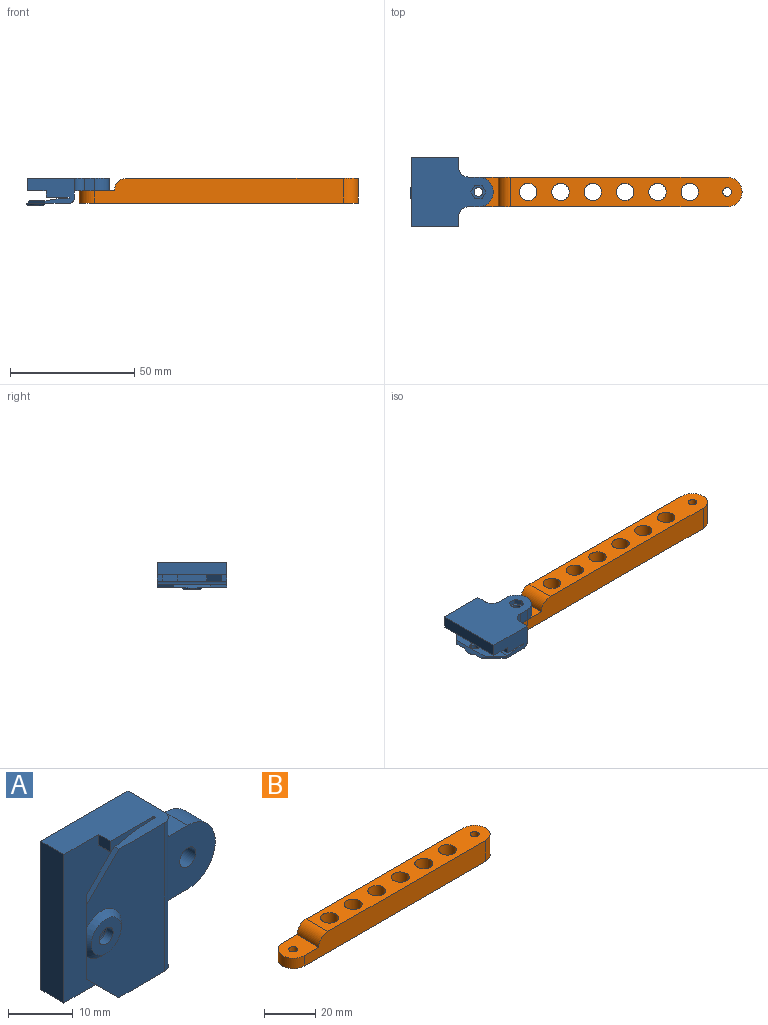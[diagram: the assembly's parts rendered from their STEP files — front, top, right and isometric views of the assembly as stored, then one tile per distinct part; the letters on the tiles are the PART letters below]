
ASSEMBLY  parts=2 mates=1
PART A: 40 faces, bbox 34x11x28 mm
  f0: plane 19x10mm, normal (0,0,1), area 144.9mm2, adj f2,f3,f5,f6,f7,f11,f13,f15
  f1: plane 19x10mm, normal (0,0,-1), area 144.9mm2, adj f2,f3,f5,f6,f7,f12,f13,f15
  f2: plane 33x28mm, normal (0,1,0), area 668mm2, adj f0,f1,f5,f15,f16,f17,f18,f20
  f3: plane 28x17mm, normal (0,-1,0), area 374mm2, adj f0,f1,f29,f30,f35,f37,f39
  f4: cylinder r=1.75mm len=3.5mm, axis (0,-1,0), area 33mm2, adj f19,f28
  f5: plane 28x5mm, normal (-1,0,0), area 140mm2, adj f0,f1,f2,f13
  f6: plane 28x9.2mm, normal (0,-1,0), area 151.4mm2, adj f0,f1,f8,f9,f10,f11,f12,f33
  f7: plane 28x0mm, normal (-1,0,0), area 0mm2, adj f0,f1,f33,f34
  f8: plane 6x5.9mm, normal (-0.71,0,0.7), area 21.9mm2, adj f6,f9,f12,f13
  f9: plane 12x2.6mm, normal (-1,0,0), area 31.2mm2, adj f6,f8,f10,f13
  f10: plane 6x5.9mm, normal (-0.71,0,-0.7), area 21.9mm2, adj f6,f9,f11,f13
  f11: plane 2.6x2mm, normal (-1,0,0), area 5.2mm2, adj f0,f6,f10,f13
  f12: plane 2.6x2mm, normal (-1,0,0), area 5.2mm2, adj f1,f6,f8,f13
  f13: plane 28x13.5mm, normal (0,-1,0), area 319mm2, adj f0,f1,f5,f8,f9,f10,f11,f12
  f14: cylinder r=1.5mm len=3mm, axis (0,-1,0), area 14.1mm2, adj f36,f38
  f15: plane 28x8mm, normal (1,0,0), area 124mm2, adj f0,f1,f2,f19,f20,f21,f37
  f16: cylinder r=6mm len=12mm, axis (0,-1,0), area 94.2mm2, adj f2,f17,f18,f19
  f17: plane 5x4mm, normal (0,0,-1), area 20mm2, adj f2,f16,f19,f21
  f18: plane 5x4mm, normal (0,0,1), area 20mm2, adj f2,f16,f19,f20
  f19: plane 20x14mm, normal (0,-1,0), area 149.8mm2, adj f4,f15,f16,f17,f18,f20,f21
  f20: cylinder r=4mm len=5mm, axis (0,-1,0), area 31.4mm2, adj f2,f15,f18,f19
  f21: cylinder r=4mm len=5mm, axis (0,1,0), area 31.4mm2, adj f2,f15,f17,f19
  f22: plane 2.6x2mm, normal (-0.87,0,0.5), area 6mm2, adj f2,f23,f27,f28
  f23: plane 2.6x2mm, normal (-0.87,0,-0.5), area 6mm2, adj f2,f22,f24,f28
  f24: plane 3x2mm, normal (0,0,-1), area 6mm2, adj f2,f23,f25,f28
  f25: plane 2.6x2mm, normal (0.87,0,-0.5), area 6mm2, adj f2,f24,f26,f28
  f26: plane 2.6x2mm, normal (0.87,0,0.5), area 6mm2, adj f2,f25,f27,f28
  f27: plane 3x2mm, normal (0,0,1), area 6mm2, adj f2,f22,f26,f28
  f28: plane 6x5.2mm, normal (0,1,0), area 13.8mm2, adj f4,f22,f23,f24,f25,f26,f27
  f29: plane 7x7mm, normal (-0.71,0,-0.71), area 9.2mm2, adj f1,f3,f31,f35
  f30: plane 7x7mm, normal (-0.71,0,0.71), area 9.2mm2, adj f0,f3,f31,f35
  f31: plane 28x6.6mm, normal (0,1,0), area 136.2mm2, adj f0,f1,f29,f30,f32,f35,f36
  f32: cylinder r=44.42mm len=28mm, axis (0,0,-1), area 259.6mm2, adj f0,f1,f31,f34
  f33: cylinder r=0.2mm len=28mm, axis (0,0,-1), area 8.8mm2, adj f0,f1,f6,f7
  f34: cylinder r=0.2mm len=28mm, axis (0,0,-1), area 8.8mm2, adj f0,f1,f7,f32
  f35: plane 16x1.5mm, normal (-0.71,0.71,0), area 23.8mm2, adj f3,f29,f30,f31,f39
  f36: torus R=2mm, axis (0,-1,0), area 8.3mm2, adj f14,f31
  f37: cylinder r=2mm len=28mm, axis (0,0,1), area 88mm2, adj f0,f1,f3,f15
  f38: plane 6.5x6.5mm, normal (0,-1,0), area 26.1mm2, adj f14,f39
  f39: cone r=3.25mm half-angle=45deg, axis (0,1,0), area 30.6mm2, adj f3,f35,f38
PART B: 18 faces, bbox 112x12x10 mm
  f0: cylinder r=6mm len=12mm, axis (0,0,-1), area 94.2mm2, adj f1,f3,f4,f5
  f1: plane 100x10mm, normal (0,-1,0), area 954.6mm2, adj f0,f4,f5,f6,f14,f15
  f2: cylinder r=1.75mm len=5mm, axis (0,0,-1), area 55mm2, adj f4,f5
  f3: plane 100x10mm, normal (0,1,0), area 954.6mm2, adj f0,f4,f5,f6,f14,f15
  f4: plane 14x12mm, normal (0,0,1), area 142.9mm2, adj f0,f1,f2,f3,f15
  f5: plane 112x12mm, normal (0,0,-1), area 1039.4mm2, adj f0,f1,f2,f3,f6,f7,f8,f9
  f6: cylinder r=6mm len=12mm, axis (0,0,-1), area 188.5mm2, adj f1,f3,f5,f14
  f7: cylinder r=3.5mm len=10mm, axis (0,0,-1), area 219.9mm2, adj f5,f14
  f8: cylinder r=3.5mm len=10mm, axis (0,0,-1), area 219.9mm2, adj f5,f14
  f9: cylinder r=3.5mm len=10mm, axis (0,0,-1), area 219.9mm2, adj f5,f14
  f10: cylinder r=3.5mm len=10mm, axis (0,0,-1), area 219.9mm2, adj f5,f14
  f11: cylinder r=3.5mm len=10mm, axis (0,0,-1), area 219.9mm2, adj f5,f14
  f12: cylinder r=3.5mm len=10mm, axis (0,0,-1), area 219.9mm2, adj f5,f14
  f13: cylinder r=1.75mm len=7mm, axis (0,0,-1), area 77mm2, adj f14,f17
  f14: plane 93x12mm, normal (0,0,1), area 860mm2, adj f1,f3,f6,f7,f8,f9,f10,f11
  f15: cylinder r=5mm len=12mm, axis (0,1,0), area 94.2mm2, adj f1,f3,f4,f14
  f16: cylinder r=3.25mm len=6.5mm, axis (0,0,1), area 61.3mm2, adj f5,f17
  f17: plane 6.5x6.5mm, normal (0,0,-1), area 23.6mm2, adj f13,f16
PLACE A rot(axis=(1,0,0),90deg) t=(-37.6,31.9,14.71)mm
PLACE B t=(19.91,17.9,9.71)mm
MATE revolute A.f4 <-> B.f0  axis (0,0,-1) through (-27.1,17.9,14.71)mm
